# Revit family: Table-Teknion-Zones_ZNTCS_Soft_Square_Canteen_Table-R2018
name_source: partatom
category: Furniture
revit_build: Autodesk Revit 2018 (Build: 20190510_1515(x64)
units: mm (PartAtom-declared; Revit-internal decimal feet)

## family parameters
Always vertical = Yes
Cut with Voids When Loaded = No
OmniClass Number = 23.40.70.14.64.21
OmniClass Title = Systems Furniture
Room Calculation Point = No
Shared = Yes
Work Plane-Based = No

## types (3) — shared parameters
Assembly Code = E2020200
Auxiliary Depth = 9 1/2"
Manufacturer = Teknion
Manufacturer Fax = 416.661.4586
Part Number = ZNTCS
Product Documentation Link = http://www.teknion.com
Product Line = Zones
Product Page URL = http://www.teknion.com
Series = Zones
Sustainability Data = http://www.teknion.com
URL = www.teknion.com
Warranty = http://www.teknion.com

## per-type parameters (varying)
| type | Bar Leg | Counter Leg | Description | Height | Model | Task Leg |
| Bar | Yes | No | Soft Square Canteen Table - Bar Height | 42" | ZNTCSB_ | No |
| Counter | No | Yes | Soft Square Canteen Table - Counter Height | 36" | ZNTCSC_ | No |
| Task | No | No | Soft Square Canteen Table - Task Height | 29" | ZNTCST_ | Yes |

## geometry (parser evidence)
native form markers: Blend x15, Sweep x4
no freeform markers — native parametric forms only
